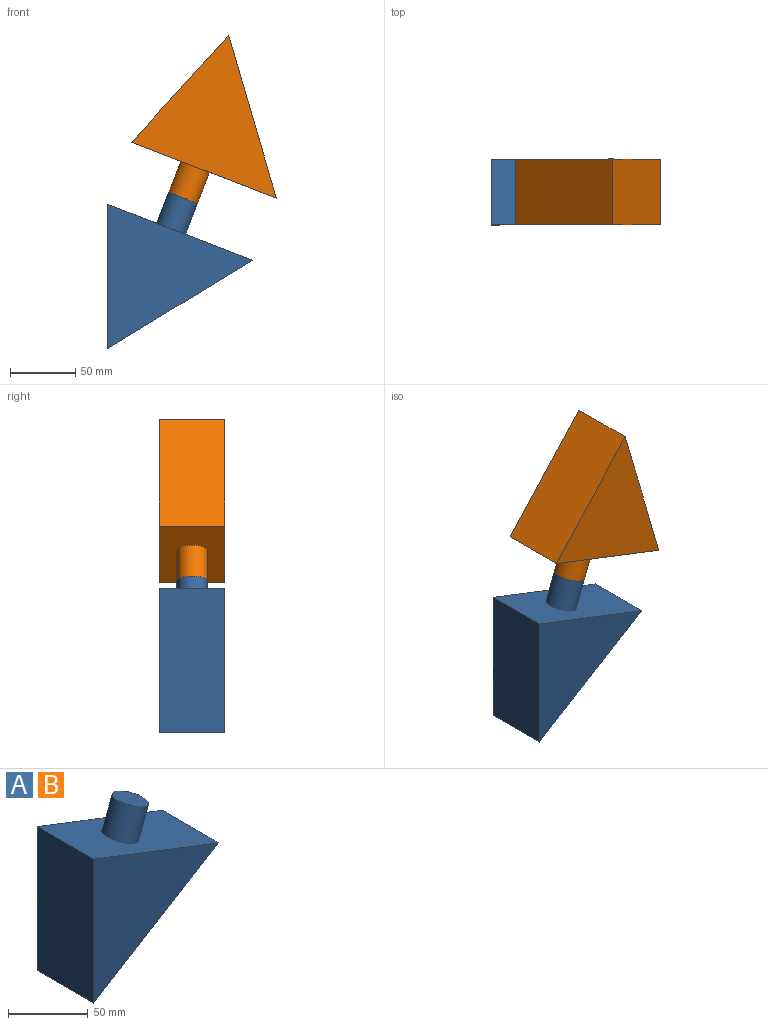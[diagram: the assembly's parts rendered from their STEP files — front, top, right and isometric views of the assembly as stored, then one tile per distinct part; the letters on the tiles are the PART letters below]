
ASSEMBLY  parts=2 mates=1
PART A: 7 faces, bbox 110.7x50x119.5 mm
  f0: plane 110.66x50mm, normal (0.36,0,0.93), area 5492.2mm2, adj f1,f2,f3,f4,f5
  f1: plane 110.29x50mm, normal (-1,0,0), area 5514.5mm2, adj f0,f2,f3,f4
  f2: plane 110.66x67.5mm, normal (0.52,0,-0.85), area 6481.1mm2, adj f0,f1,f3,f4
  f3: plane 110.66x110.29mm, normal (0,-1,0), area 6102.3mm2, adj f0,f1,f2
  f4: plane 110.66x110.29mm, normal (0,1,0), area 6102.3mm2, adj f0,f1,f2
  f5: cylinder r=11.83mm len=32.23mm, axis (-0.36,0,-0.93), area 1888.8mm2, adj f0,f6
  f6: plane 23.67x22.08mm, normal (0.36,0,0.93), area 440mm2, adj f5
PART B: same geometry as A
PLACE A t=(-116.15,-123.33,-50.7)mm
PLACE B rot(axis=(0.93,0,-0.36),180deg) t=(-76.58,-123.33,51.65)mm
MATE fastened A.f5 <-> B.f5  axis (0.36,0,0.93) through (-107.11,-123.33,4.63)mm
